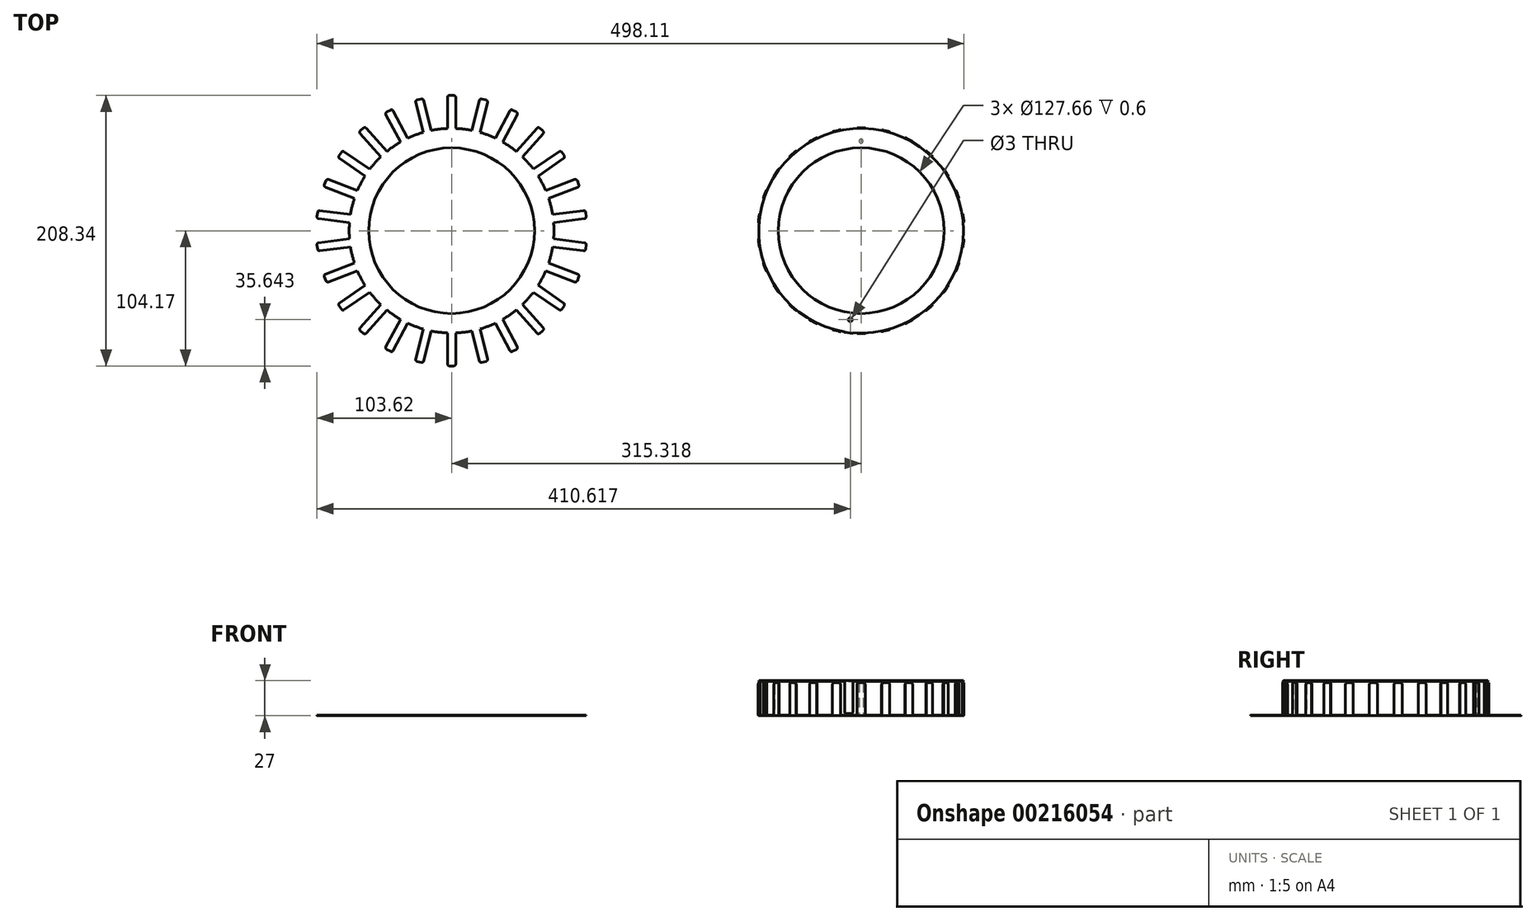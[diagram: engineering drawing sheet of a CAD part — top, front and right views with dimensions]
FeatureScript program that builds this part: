
annotation { "Feature Type Name" : "Feature", "Feature Type Description" : "" }
export const myFeature = defineFeature(function(context is Context, id is Id, definition is map)
    precondition{}
    {
        {
            assignVariable(context, id + "F0", {"name" : "NumFingers", "anyValue" : 26});
        }
        {
            var Q0;
            Q0=qCreatedBy(makeId("Top.planeOp"),FACE);
            var sketch = newSketch(context, id + "F1", { "sketchPlane" : qUnion([Q0])});
            skLineSegment(sketch, "E0", {"start": v(0, 0) * mm, "end": v(0, 78.77) * mm, "construction": true});
            skPoint(sketch, "E1.center", {"position": v(0, 0) * mm});
            skLineSegment(sketch, "E2.bottom", {"start": v(1.67, 104.17) * mm, "end": v(-1.67, 104.17) * mm});
            skLineSegment(sketch, "E2.top", {"start": v(3.17, 78.77) * mm, "end": v(-3.17, 78.77) * mm, "construction": true});
            skLineSegment(sketch, "E2.left", {"start": v(3.18, 102.67) * mm, "end": v(3.18, 78.77) * mm});
            skLineSegment(sketch, "E2.right", {"start": v(-3.17, 102.67) * mm, "end": v(-3.17, 78.77) * mm});
            skPoint(sketch, "E3", {"position": v(0, 78.77) * mm});
            skLineSegment(sketch, "E4", {"start": v(-3.18, 78.77) * mm, "end": v(0, 0) * mm, "construction": true});
            skArc(sketch, "E5", {"start": v(-3.18, 78.77) * mm, "mid": v(0, -78.83) * mm, "end": v(3.17, 78.77) * mm});
            skPoint(sketch, "E6.visualSharp", {"position": v(-3.17, 104.17) * mm});
            skArc(sketch, "E6.filletArc", {"start": v(-1.67, 104.17) * mm, "mid": v(-2.74, 103.73) * mm, "end": v(-3.17, 102.67) * mm});
            skPoint(sketch, "E7.visualSharp", {"position": v(3.17, 104.17) * mm});
            skArc(sketch, "E7.filletArc", {"start": v(3.17, 102.67) * mm, "mid": v(2.74, 103.73) * mm, "end": v(1.67, 104.17) * mm});
            skCircle(sketch, "E8", {"center": v(0, 0) * mm, "radius": 63.83 * mm});
            skSolve(sketch);
        }
        {
            var Q0;
            Q0=makeQuery(id+"F1.imprint","IMPRINT",FACE,{"disambiguationData":[TD([[makeQuery(id+"F1.imprint","IMPRINT",EDGE,{"derivedFrom":sQuery(id+"F1.wireOp",EDGE,"E2.bottom")}),1.0]])]});
            var Q1;
            {var subQ0=sQuery(id+"F1.wireOp",EDGE,"E2.top");Q1=makeQuery(id+"F1.imprint","IMPRINT",FACE,{"disambiguationData":[TD([[makeQuery(id+"F1.imprint","IMPRINT",EDGE,{"derivedFrom":subQ0}),1.0]])]});}
            var Q2;
            Q2=sQuery(id+"F1.wireOp",EDGE,"hmrcqJ3q-lU7G-KxSF-X1eN-bNX01pqxhZci");
            var Q3;
            Q3=sQuery(id+"F1.wireOp",EDGE,"hotj8Gxh-6EDq-oSzS-3hbz-jsD0qoGDDY39");
            extrude(context, id + "F2", {"entities" : qUnion([Q0, Q1]), "surfaceEntities" : qUnion([Q2, Q3]), "depth" : .6 * mm});
        }
        {
            var Q0;
            Q0=qCreatedBy(makeId("Right.planeOp"),FACE);
            var sketch = newSketch(context, id + "F3", { "sketchPlane" : qUnion([Q0])});
            skLineSegment(sketch, "E9", {"start": v(0, 49.5) * mm, "end": v(0, -49.5) * mm, "construction": true});
            skSolve(sketch);
        }
        {
            var Q0;
            Q0=makeQuery(id+"F2.opExtrude","SWEPT_BODY",BODY,{"disambiguationData":[OSD([sQuery(id+"F1.wireOp",EDGE,"E2.bottom"),sQuery(id+"F1.wireOp",EDGE,"E2.top"),sQuery(id+"F1.wireOp",EDGE,"E2.left"),sQuery(id+"F1.wireOp",EDGE,"E2.right")])]});
            var Q1;
            Q1=sQuery(id+"F3.wireOp",EDGE,"E9");
            circularPattern(context, id + "F4", {"operationType" : NewBodyOperationType.ADD, "entities" : qUnion([Q0]), "axis" : qUnion([Q1]), "angle" : 360 * degree, "instanceCount" : getVariable(context, 'NumFingers'), "equalSpace" : true});
        }
        {
            var Q0;
            Q0=qCreatedBy(makeId("Top.planeOp"),FACE);
            var sketch = newSketch(context, id + "F5", { "sketchPlane" : qUnion([Q0])});
            skLineSegment(sketch, "E10", {"start": v(315.32, 0) * mm, "end": v(315.32, 78.77) * mm, "construction": true});
            skPoint(sketch, "E11.center", {"position": v(315.32, 0) * mm});
            skLineSegment(sketch, "E12.bottom", {"start": v(318.5, 79.37) * mm, "end": v(312.14, 79.37) * mm});
            skLineSegment(sketch, "E12.top", {"start": v(318.5, 78.77) * mm, "end": v(312.14, 78.77) * mm, "construction": true});
            skLineSegment(sketch, "E12.left", {"start": v(318.5, 79.37) * mm, "end": v(318.5, 78.77) * mm});
            skLineSegment(sketch, "E12.right", {"start": v(312.14, 79.37) * mm, "end": v(312.14, 78.77) * mm});
            skPoint(sketch, "E13", {"position": v(315.32, 78.77) * mm});
            skLineSegment(sketch, "E14", {"start": v(312.14, 78.77) * mm, "end": v(315.32, 0) * mm, "construction": true});
            skArc(sketch, "E15", {"start": v(312.14, 78.77) * mm, "mid": v(315.32, -78.83) * mm, "end": v(318.5, 78.77) * mm});
            skPoint(sketch, "E16.visualSharp", {"position": v(312.14, 79.37) * mm});
            skCircle(sketch, "E17", {"center": v(315.32, 0) * mm, "radius": 63.83 * mm});
            skLineSegment(sketch, "E18", {"start": v(0, 0) * mm, "end": v(315.32, 0) * mm, "construction": true});
            skLineSegment(sketch, "E19", {"start": v(318.5, 78.77) * mm, "end": v(312.14, 78.77) * mm});
            skCircle(sketch, "E20", {"center": v(315.32, 69.03) * mm, "radius": 1.5 * mm});
            skSolve(sketch);
        }
        {
            var Q0;
            Q0=makeQuery(id+"F5.imprint","IMPRINT",FACE,{"disambiguationData":[TD([[makeQuery(id+"F5.imprint","IMPRINT",EDGE,{"derivedFrom":sQuery(id+"F5.wireOp",EDGE,"E15")}),1.0]])]});
            extrude(context, id + "F6", {"entities" : qUnion([Q0]), "depth" : 0.6 * mm});
        }
        {
            var Q0;
            Q0=makeQuery(id+"F5.imprint","IMPRINT",FACE,{"disambiguationData":[TD([[makeQuery(id+"F5.imprint","IMPRINT",EDGE,{"derivedFrom":sQuery(id+"F5.wireOp",EDGE,"E12.bottom")}),1.0]])]});
            extrude(context, id + "F7", {"entities" : qUnion([Q0]), "operationType" : NewBodyOperationType.ADD, "depth" : 25.4 * mm});
        }
        {
            var Q0;
            Q0=makeQuery(id+"F7.opExtrude","CAP_EDGE",EDGE,{"disambiguationData":[OSD([sQuery(id+"F5.wireOp",EDGE,"E12.right")])],"isStart":false});
            var Q1;
            Q1=makeQuery(id+"F7.opExtrude","CAP_EDGE",EDGE,{"disambiguationData":[OSD([sQuery(id+"F5.wireOp",EDGE,"E12.left")])],"isStart":false});
            fillet(context, id + "F8", {"entities" : qUnion([Q0, Q1]), "radius" : 1.5 * mm, "tangentPropagation" : true, "allowEdgeOverflow" : false});
        }
        {
            var Q0;
            Q0=makeQuery(id+"F7.opExtrude","CAP_EDGE",EDGE,{"disambiguationData":[OSD([sQuery(id+"F5.wireOp",EDGE,"E12.bottom")])],"isStart":true});
            fillet(context, id + "F9", {"entities" : qUnion([Q0]), "radius" : .6 * mm, "tangentPropagation" : true, "allowEdgeOverflow" : false});
        }
        {
            var Q0;
            Q0=makeQuery(id+"F7.opExtrude","CAP_EDGE",EDGE,{"disambiguationData":[OSD([sQuery(id+"F5.wireOp",EDGE,"E19")])],"isStart":false});
            cPoint(context, id + "F10", {"entities" : qUnion([Q0]), "parameter" : 0.5});
        }
        {
            var Q0;
            Q0=sQuery(id+"F5.wireOp",EDGE,"E10");
            var Q1;
            Q1 = qCreatedBy(id + "F10" ,VERTEX);
            cPlane(context, id + "F11", {"entities" : qUnion([Q0, Q1]), "cplaneType" : CPlaneType.LINE_ANGLE, "offset" : 25 * mm, "angle" : 0 * degree, "width" : 150 * mm, "height" : 150 * mm});
        }
        {
            var Q0;
            Q0=qCreatedBy(id+"F11.planeOp",FACE);
            var sketch = newSketch(context, id + "F12", { "sketchPlane" : qUnion([Q0])});
            skLineSegment(sketch, "E21", {"start": v(0, -117.76) * mm, "end": v(0, 117.76) * mm, "construction": true});
            skPoint(sketch, "E22", {"position": v(0, 0) * mm});
            skSolve(sketch);
        }
        {
            var Q0;
            Q0=makeQuery(id+"F6.opExtrude","SWEPT_BODY",BODY,{"disambiguationData":[OSD([sQuery(id+"F5.wireOp",EDGE,"E15"),sQuery(id+"F5.wireOp",EDGE,"E17"),sQuery(id+"F5.wireOp",EDGE,"E19")])]});
            var Q1;
            Q1=sQuery(id+"F12.wireOp",EDGE,"E21");
            circularPattern(context, id + "F13", {"operationType" : NewBodyOperationType.ADD, "entities" : qUnion([Q0]), "axis" : qUnion([Q1]), "angle" : 360 * degree, "instanceCount" : getVariable(context, 'NumFingers'), "equalSpace" : true});
        }
        {
            var Q0;
            Q0=makeQuery(id+"F6.opExtrude","SWEPT_BODY",BODY,{"disambiguationData":[OSD([sQuery(id+"F5.wireOp",EDGE,"E15"),sQuery(id+"F5.wireOp",EDGE,"E17"),sQuery(id+"F5.wireOp",EDGE,"E19")])]});
            var Q1;
            Q1=makeQuery(id+"F6.opExtrude","CAP_EDGE",EDGE,{"disambiguationData":[OSD([sQuery(id+"F5.wireOp",EDGE,"E17")])],"isStart":false});
            transform(context, id + "F14", {"entities" : qUnion([Q0]), "transformType" : TransformType.ROTATION, "transformAxis" : qUnion([Q1]), "angle" : (180 / getVariable(context, 'NumFingers')) * degree, "makeCopy" : true});
        }
        {
            var Q0;
            Q0=makeQuery(id+"F14.opPattern","COPY",BODY,{"derivedFrom":makeQuery(id+"F6.opExtrude","SWEPT_BODY",BODY,{"disambiguationData":[OSD([sQuery(id+"F5.wireOp",EDGE,"E15"),sQuery(id+"F5.wireOp",EDGE,"E17"),sQuery(id+"F5.wireOp",EDGE,"E19")])]}),"instanceName":"1"});
            var Q1;
            Q1=sQuery(id+"F5.wireOp",EDGE,"E18");
            transform(context, id + "F15", {"entities" : qUnion([Q0]), "transformType" : TransformType.ROTATION, "transformAxis" : qUnion([Q1]), "angle" : 180 * degree, "makeCopy" : false});
        }
        {
            var Q0;
            Q0=makeQuery(id+"F14.opPattern","COPY",BODY,{"derivedFrom":makeQuery(id+"F6.opExtrude","SWEPT_BODY",BODY,{"disambiguationData":[OSD([sQuery(id+"F5.wireOp",EDGE,"E15"),sQuery(id+"F5.wireOp",EDGE,"E17"),sQuery(id+"F5.wireOp",EDGE,"E19")])]}),"instanceName":"1"});
            var Q1;
            Q1=sQuery(id+"F12.wireOp",EDGE,"E21");
            transform(context, id + "F16", {"entities" : qUnion([Q0]), "transformType" : TransformType.TRANSLATION_DISTANCE, "transformDirection" : qUnion([Q1]), "distance" : 27 * mm, "makeCopy" : false});
        }
        {
            var Q0;
            Q0=makeQuery(id+"F5.imprint","IMPRINT",FACE,{"disambiguationData":[TD([[makeQuery(id+"F5.imprint","IMPRINT",EDGE,{"derivedFrom":sQuery(id+"F5.wireOp",EDGE,"E20")}),1.0]])]});
            var Q1;
            {var subQ0=makeQuery(id+"F6.opExtrude","CAP_FACE",FACE,{"disambiguationData":[OSD([sQuery(id+"F5.wireOp",EDGE,"E15"),sQuery(id+"F5.wireOp",EDGE,"E17"),sQuery(id+"F5.wireOp",EDGE,"E19"),sQuery(id+"F5.wireOp",EDGE,"E20")])],"isStart":false});Q1=makeQuery(id+"F14.opPattern","COPY",FACE,{"derivedFrom":makeQuery(id+"F13.boolean.opBoolean","MERGE",FACE,{"derivedFrom":[subQ0,makeQuery(id+"F13.opPattern","COPY",FACE,{"derivedFrom":subQ0,"instanceName":"1"}),makeQuery(id+"F13.opPattern","COPY",FACE,{"derivedFrom":subQ0,"instanceName":"2"}),makeQuery(id+"F13.opPattern","COPY",FACE,{"derivedFrom":subQ0,"instanceName":"3"}),makeQuery(id+"F13.opPattern","COPY",FACE,{"derivedFrom":subQ0,"instanceName":"4"}),makeQuery(id+"F13.opPattern","COPY",FACE,{"derivedFrom":subQ0,"instanceName":"5"}),makeQuery(id+"F13.opPattern","COPY",FACE,{"derivedFrom":subQ0,"instanceName":"6"}),makeQuery(id+"F13.opPattern","COPY",FACE,{"derivedFrom":subQ0,"instanceName":"7"}),makeQuery(id+"F13.opPattern","COPY",FACE,{"derivedFrom":subQ0,"instanceName":"8"}),makeQuery(id+"F13.opPattern","COPY",FACE,{"derivedFrom":subQ0,"instanceName":"9"}),makeQuery(id+"F13.opPattern","COPY",FACE,{"derivedFrom":subQ0,"instanceName":"10"}),makeQuery(id+"F13.opPattern","COPY",FACE,{"derivedFrom":subQ0,"instanceName":"11"}),makeQuery(id+"F13.opPattern","COPY",FACE,{"derivedFrom":subQ0,"instanceName":"12"}),makeQuery(id+"F13.opPattern","COPY",FACE,{"derivedFrom":subQ0,"instanceName":"13"}),makeQuery(id+"F13.opPattern","COPY",FACE,{"derivedFrom":subQ0,"instanceName":"14"}),makeQuery(id+"F13.opPattern","COPY",FACE,{"derivedFrom":subQ0,"instanceName":"15"}),makeQuery(id+"F13.opPattern","COPY",FACE,{"derivedFrom":subQ0,"instanceName":"16"}),makeQuery(id+"F13.opPattern","COPY",FACE,{"derivedFrom":subQ0,"instanceName":"17"}),makeQuery(id+"F13.opPattern","COPY",FACE,{"derivedFrom":subQ0,"instanceName":"18"}),makeQuery(id+"F13.opPattern","COPY",FACE,{"derivedFrom":subQ0,"instanceName":"19"}),makeQuery(id+"F13.opPattern","COPY",FACE,{"derivedFrom":subQ0,"instanceName":"20"}),makeQuery(id+"F13.opPattern","COPY",FACE,{"derivedFrom":subQ0,"instanceName":"21"}),makeQuery(id+"F13.opPattern","COPY",FACE,{"derivedFrom":subQ0,"instanceName":"22"}),makeQuery(id+"F13.opPattern","COPY",FACE,{"derivedFrom":subQ0,"instanceName":"23"}),makeQuery(id+"F13.opPattern","COPY",FACE,{"derivedFrom":subQ0,"instanceName":"24"}),makeQuery(id+"F13.opPattern","COPY",FACE,{"derivedFrom":subQ0,"instanceName":"25"}),makeQuery(id+"F13.opPattern","COPY",FACE,{"derivedFrom":subQ0,"instanceName":"26"}),makeQuery(id+"F13.opPattern","COPY",FACE,{"derivedFrom":subQ0,"instanceName":"27"}),makeQuery(id+"F13.opPattern","COPY",FACE,{"derivedFrom":subQ0,"instanceName":"28"}),makeQuery(id+"F13.opPattern","COPY",FACE,{"derivedFrom":subQ0,"instanceName":"29"}),makeQuery(id+"F13.opPattern","COPY",FACE,{"derivedFrom":subQ0,"instanceName":"30"}),makeQuery(id+"F13.opPattern","COPY",FACE,{"derivedFrom":subQ0,"instanceName":"31"})]}),"instanceName":"1"});}
            extrude(context, id + "F17", {"entities" : qUnion([Q0]), "operationType" : NewBodyOperationType.ADD, "endBound" : BoundingType.UP_TO_SURFACE, "endBoundEntityFace" : qUnion([Q1]), "depth" : 25 * mm});
        }
    });
